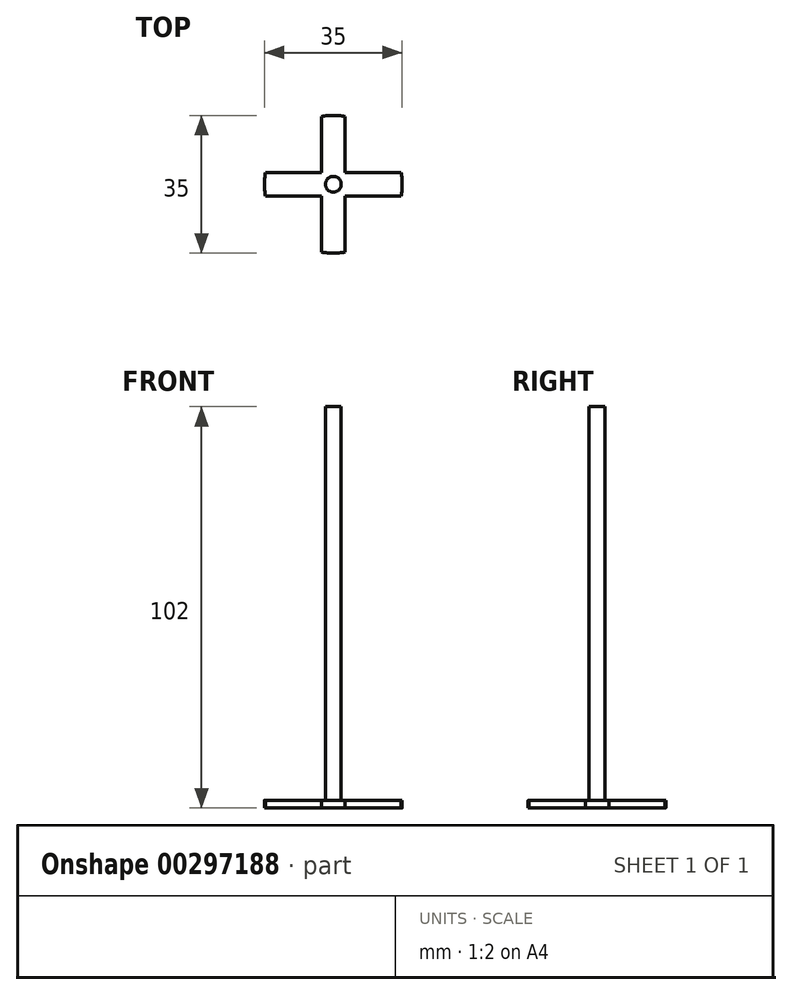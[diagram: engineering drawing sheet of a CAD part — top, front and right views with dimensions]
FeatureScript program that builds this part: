
annotation { "Feature Type Name" : "Feature", "Feature Type Description" : "" }
export const myFeature = defineFeature(function(context is Context, id is Id, definition is map)
    precondition{}
    {
        {
            var Q0;
            Q0=qCreatedBy(makeId("Top.planeOp"),FACE);
            var sketch = newSketch(context, id + "F0", { "sketchPlane" : qUnion([Q0])});
            skArc(sketch, "E0", {"start": v(3, 17.24) * mm, "mid": v(0, 17.5) * mm, "end": v(-3, 17.24) * mm});
            skLineSegment(sketch, "E1", {"start": v(-17.24, -3) * mm, "end": v(-3, -3) * mm});
            skLineSegment(sketch, "E2", {"start": v(-17.24, 3) * mm, "end": v(-3, 3) * mm});
            skLineSegment(sketch, "E3", {"start": v(-3, -17.24) * mm, "end": v(-3, -3) * mm});
            skLineSegment(sketch, "E4", {"start": v(3, -17.24) * mm, "end": v(3, -3) * mm});
            skLineSegment(sketch, "E5.trimOffspring", {"start": v(-3, 3) * mm, "end": v(-3, 17.24) * mm});
            skLineSegment(sketch, "E6.trimOffspring", {"start": v(3, 3) * mm, "end": v(17.24, 3) * mm});
            skLineSegment(sketch, "E7.trimOffspring", {"start": v(3, 3) * mm, "end": v(3, 17.24) * mm});
            skLineSegment(sketch, "E8.trimOffspring", {"start": v(3, -3) * mm, "end": v(17.24, -3) * mm});
            skArc(sketch, "E9.trimOffspring", {"start": v(17.24, -3) * mm, "mid": v(17.5, 0) * mm, "end": v(17.24, 3) * mm});
            skArc(sketch, "E10.trimOffspring", {"start": v(-3, -17.24) * mm, "mid": v(0, -17.5) * mm, "end": v(3, -17.24) * mm});
            skArc(sketch, "E11.trimOffspring", {"start": v(-17.24, 3) * mm, "mid": v(-17.5, 0) * mm, "end": v(-17.24, -3) * mm});
            skSolve(sketch);
        }
        {
            var Q0;
            Q0 = qSketchRegion(id + "F0", true);
            extrude(context, id + "F1", {"entities" : qUnion([Q0]), "depth" : 2 * mm});
        }
        {
            var Q0;
            Q0=makeQuery(id+"F1.opExtrude","CAP_FACE",FACE,{"disambiguationData":[OSD([sQuery(id+"F0.wireOp",EDGE,"E0"),sQuery(id+"F0.wireOp",EDGE,"E1"),sQuery(id+"F0.wireOp",EDGE,"E2"),sQuery(id+"F0.wireOp",EDGE,"E3"),sQuery(id+"F0.wireOp",EDGE,"E4"),sQuery(id+"F0.wireOp",EDGE,"E5.trimOffspring"),sQuery(id+"F0.wireOp",EDGE,"E6.trimOffspring"),sQuery(id+"F0.wireOp",EDGE,"E7.trimOffspring"),sQuery(id+"F0.wireOp",EDGE,"E8.trimOffspring"),sQuery(id+"F0.wireOp",EDGE,"E9.trimOffspring"),sQuery(id+"F0.wireOp",EDGE,"E10.trimOffspring"),sQuery(id+"F0.wireOp",EDGE,"E11.trimOffspring")])],"isStart":false});
            var sketch = newSketch(context, id + "F2", { "sketchPlane" : qUnion([Q0])});
            skCircle(sketch, "E12", {"center": v(0, 0) * mm, "radius": 2 * mm});
            skSolve(sketch);
        }
        {
            var Q0;
            Q0 = qSketchRegion(id + "F2", true);
            extrude(context, id + "F3", {"entities" : qUnion([Q0]), "operationType" : NewBodyOperationType.ADD, "depth" : 100 * mm});
        }
    });
